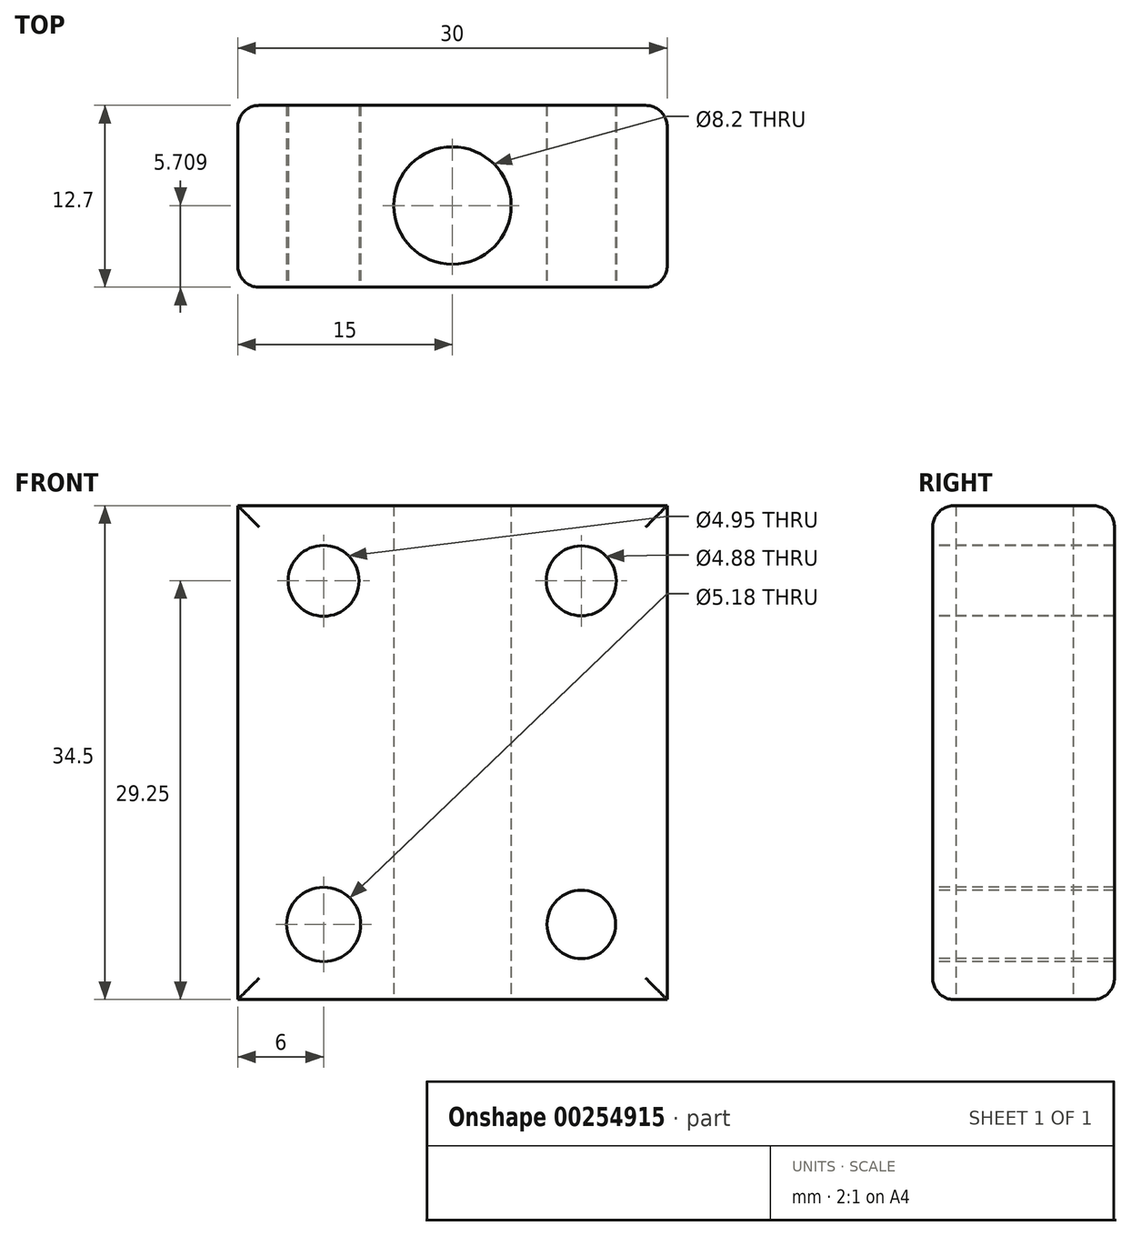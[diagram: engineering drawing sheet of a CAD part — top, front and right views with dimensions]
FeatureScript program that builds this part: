
annotation { "Feature Type Name" : "Feature", "Feature Type Description" : "" }
export const myFeature = defineFeature(function(context is Context, id is Id, definition is map)
    precondition{}
    {
        {
            var Q0;
            Q0=qCreatedBy(makeId("Front.planeOp"),FACE);
            var sketch = newSketch(context, id + "F0", { "sketchPlane" : qUnion([Q0])});
            skLineSegment(sketch, "E0.bottom", {"start": v(15, -17.25) * mm, "end": v(-15, -17.25) * mm});
            skLineSegment(sketch, "E0.top", {"start": v(15, 17.25) * mm, "end": v(-15, 17.25) * mm});
            skLineSegment(sketch, "E0.left", {"start": v(15, -17.25) * mm, "end": v(15, 17.25) * mm});
            skLineSegment(sketch, "E0.right", {"start": v(-15, -17.25) * mm, "end": v(-15, 17.25) * mm});
            skPoint(sketch, "E0.middle", {"position": v(0, 0) * mm});
            skSolve(sketch);
        }
        {
            var Q0;
            Q0 = qSketchRegion(id + "F0", true);
            extrude(context, id + "F1", {"entities" : qUnion([Q0]), "depth" : 12.7 * mm});
        }
        {
            var Q0;
            Q0=makeQuery(id+"F1.opExtrude","CAP_FACE",FACE,{"disambiguationData":[OSD([sQuery(id+"F0.wireOp",EDGE,"E0.bottom"),sQuery(id+"F0.wireOp",EDGE,"E0.top"),sQuery(id+"F0.wireOp",EDGE,"E0.left"),sQuery(id+"F0.wireOp",EDGE,"E0.right")])],"isStart":false});
            var sketch = newSketch(context, id + "F2", { "sketchPlane" : qUnion([Q0])});
            skCircle(sketch, "E1", {"center": v(-9, 12) * mm, "radius": 2.48 * mm});
            skCircle(sketch, "E2", {"center": v(-9, -12) * mm, "radius": 2.6 * mm});
            skCircle(sketch, "E3", {"center": v(9, 12) * mm, "radius": 2.44 * mm});
            skCircle(sketch, "E4", {"center": v(9, -12) * mm, "radius": 2.4 * mm});
            skSolve(sketch);
        }
        {
            var Q0;
            Q0 = qSketchRegion(id + "F2", true);
            extrude(context, id + "F3", {"entities" : qUnion([Q0]), "operationType" : NewBodyOperationType.REMOVE, "endBound" : BoundingType.THROUGH_ALL, "oppositeDirection" : true, "depth" : 25 * mm});
        }
        {
            var Q0;
            Q0=makeQuery(id+"F1.opExtrude","CAP_EDGE",EDGE,{"disambiguationData":[OSD([sQuery(id+"F0.wireOp",EDGE,"E0.right")])],"isStart":true});
            var Q1;
            Q1=makeQuery(id+"F1.opExtrude","CAP_EDGE",EDGE,{"disambiguationData":[OSD([sQuery(id+"F0.wireOp",EDGE,"E0.top")])],"isStart":true});
            var Q2;
            Q2=makeQuery(id+"F1.opExtrude","CAP_EDGE",EDGE,{"disambiguationData":[OSD([sQuery(id+"F0.wireOp",EDGE,"E0.left")])],"isStart":true});
            var Q3;
            Q3=makeQuery(id+"F1.opExtrude","CAP_EDGE",EDGE,{"disambiguationData":[OSD([sQuery(id+"F0.wireOp",EDGE,"E0.bottom")])],"isStart":true});
            var Q4;
            Q4=makeQuery(id+"F1.opExtrude","CAP_EDGE",EDGE,{"disambiguationData":[OSD([sQuery(id+"F0.wireOp",EDGE,"E0.left")])],"isStart":false});
            var Q5;
            Q5=makeQuery(id+"F1.opExtrude","CAP_EDGE",EDGE,{"disambiguationData":[OSD([sQuery(id+"F0.wireOp",EDGE,"E0.top")])],"isStart":false});
            var Q6;
            Q6=makeQuery(id+"F1.opExtrude","CAP_EDGE",EDGE,{"disambiguationData":[OSD([sQuery(id+"F0.wireOp",EDGE,"E0.right")])],"isStart":false});
            var Q7;
            Q7=makeQuery(id+"F1.opExtrude","CAP_EDGE",EDGE,{"disambiguationData":[OSD([sQuery(id+"F0.wireOp",EDGE,"E0.bottom")])],"isStart":false});
            fillet(context, id + "F4", {"entities" : qUnion([Q0, Q1, Q2, Q3, Q4, Q5, Q6, Q7]), "radius" : 1.5 * mm, "tangentPropagation" : true, "allowEdgeOverflow" : false});
        }
        {
            var Q0;
            Q0=makeQuery(id+"F1.opExtrude","SWEPT_FACE",FACE,{"disambiguationData":[OSD([sQuery(id+"F0.wireOp",EDGE,"E0.bottom")])]});
            var sketch = newSketch(context, id + "F5", { "sketchPlane" : qUnion([Q0])});
            skCircle(sketch, "E5", {"center": v(0, 7) * mm, "radius": 4.1 * mm});
            skSolve(sketch);
        }
        {
            var Q0;
            Q0 = qSketchRegion(id + "F5", true);
            extrude(context, id + "F6", {"entities" : qUnion([Q0]), "operationType" : NewBodyOperationType.REMOVE, "endBound" : BoundingType.THROUGH_ALL, "oppositeDirection" : true, "depth" : 33 * mm});
        }
    });
